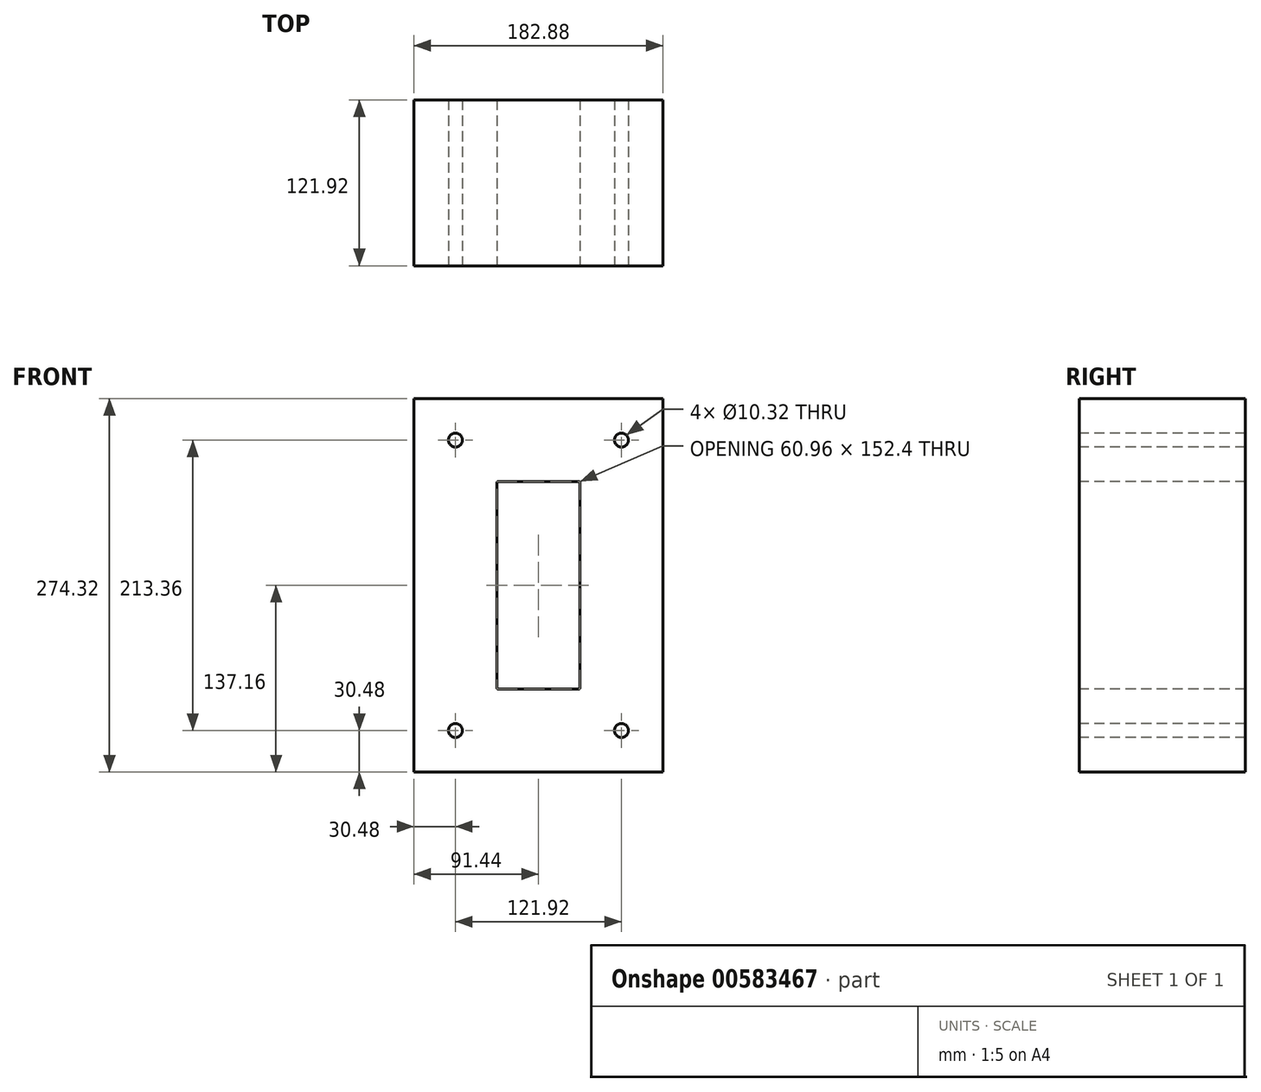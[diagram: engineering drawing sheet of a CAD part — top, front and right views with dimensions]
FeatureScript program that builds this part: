
annotation { "Feature Type Name" : "Feature", "Feature Type Description" : "" }
export const myFeature = defineFeature(function(context is Context, id is Id, definition is map)
    precondition{}
    {
        {
            assignVariable(context, id + "F0", {"name" : "StackHeight", "anyValue" : 121.92 * mm});
        }
        {
            var Q0;
            Q0=qCreatedBy(makeId("Front.planeOp"),FACE);
            var sketch = newSketch(context, id + "F1", { "sketchPlane" : qUnion([Q0])});
            skLineSegment(sketch, "E0.bottom", {"start": v(91.44, -137.16) * mm, "end": v(-91.44, -137.16) * mm});
            skLineSegment(sketch, "E0.top", {"start": v(91.44, 137.16) * mm, "end": v(-91.44, 137.16) * mm});
            skLineSegment(sketch, "E0.left", {"start": v(91.44, -137.16) * mm, "end": v(91.44, 137.16) * mm});
            skLineSegment(sketch, "E0.right", {"start": v(-91.44, -137.16) * mm, "end": v(-91.44, 137.16) * mm});
            skPoint(sketch, "E0.middle", {"position": v(0, 0) * mm});
            skSolve(sketch);
        }
        {
            var Q0;
            Q0=qSketchRegion(id+"F1",true);
            extrude(context, id + "F2", {"entities" : qUnion([Q0]), "oppositeDirection" : true, "depth" : (getVariable(context, 'StackHeight'))});
        }
        {
            var Q0;
            Q0=makeQuery(id+"F2.opExtrude","CAP_FACE",FACE,{"disambiguationData":[OSD([sQuery(id+"F1.wireOp",EDGE,"E0.bottom"),sQuery(id+"F1.wireOp",EDGE,"E0.top"),sQuery(id+"F1.wireOp",EDGE,"E0.left"),sQuery(id+"F1.wireOp",EDGE,"E0.right")])],"isStart":true});
            var sketch = newSketch(context, id + "F3", { "sketchPlane" : qUnion([Q0])});
            skCircle(sketch, "E1", {"center": v(-60.96, 106.68) * mm, "radius": 5.16 * mm});
            skCircle(sketch, "E2", {"center": v(60.96, 106.68) * mm, "radius": 5.16 * mm});
            skCircle(sketch, "E3", {"center": v(-60.96, -106.68) * mm, "radius": 5.16 * mm});
            skCircle(sketch, "E4", {"center": v(60.96, -106.68) * mm, "radius": 5.16 * mm});
            skSolve(sketch);
        }
        {
            var Q0;
            Q0=qSketchRegion(id+"F3",true);
            extrude(context, id + "F4", {"entities" : qUnion([Q0]), "operationType" : NewBodyOperationType.REMOVE, "oppositeDirection" : true, "depth" : (getVariable(context, 'StackHeight'))});
        }
        {
            var Q0;
            Q0=makeQuery(id+"F2.opExtrude","CAP_FACE",FACE,{"disambiguationData":[OSD([sQuery(id+"F1.wireOp",EDGE,"E0.bottom"),sQuery(id+"F1.wireOp",EDGE,"E0.top"),sQuery(id+"F1.wireOp",EDGE,"E0.left"),sQuery(id+"F1.wireOp",EDGE,"E0.right")])],"isStart":true});
            var sketch = newSketch(context, id + "F5", { "sketchPlane" : qUnion([Q0])});
            skLineSegment(sketch, "E5.bottom", {"start": v(-30.48, -76.2) * mm, "end": v(30.48, -76.2) * mm});
            skLineSegment(sketch, "E5.top", {"start": v(-30.48, 76.2) * mm, "end": v(30.48, 76.2) * mm});
            skLineSegment(sketch, "E5.left", {"start": v(-30.48, -76.2) * mm, "end": v(-30.48, 76.2) * mm});
            skLineSegment(sketch, "E5.right", {"start": v(30.48, -76.2) * mm, "end": v(30.48, 76.2) * mm});
            skPoint(sketch, "E5.middle", {"position": v(0, 0) * mm});
            skSolve(sketch);
        }
        {
            var Q0;
            Q0=qSketchRegion(id+"F5",true);
            extrude(context, id + "F6", {"entities" : qUnion([Q0]), "operationType" : NewBodyOperationType.REMOVE, "oppositeDirection" : true, "depth" : (getVariable(context, 'StackHeight'))});
        }
        {
            var Q0;
            Q0=makeQuery(id+"F6.boolean.opBoolean","COPY",EDGE,{"derivedFrom":makeQuery(id+"F6.opExtrude","SWEPT_EDGE",EDGE,{"disambiguationData":[OSD([sQuery(id+"F5.wireOp",EDGE,"E5.top"),sQuery(id+"F5.wireOp",EDGE,"E5.left")])]})});
            var Q1;
            Q1=makeQuery(id+"F6.boolean.opBoolean","COPY",EDGE,{"derivedFrom":makeQuery(id+"F6.opExtrude","SWEPT_EDGE",EDGE,{"disambiguationData":[OSD([sQuery(id+"F5.wireOp",EDGE,"E5.top"),sQuery(id+"F5.wireOp",EDGE,"E5.right")])]})});
            var Q2;
            Q2=makeQuery(id+"F6.boolean.opBoolean","COPY",EDGE,{"derivedFrom":makeQuery(id+"F6.opExtrude","SWEPT_EDGE",EDGE,{"disambiguationData":[OSD([sQuery(id+"F5.wireOp",EDGE,"E5.bottom"),sQuery(id+"F5.wireOp",EDGE,"E5.right")])]})});
            var Q3;
            Q3=makeQuery(id+"F6.boolean.opBoolean","COPY",EDGE,{"derivedFrom":makeQuery(id+"F6.opExtrude","SWEPT_EDGE",EDGE,{"disambiguationData":[OSD([sQuery(id+"F5.wireOp",EDGE,"E5.bottom"),sQuery(id+"F5.wireOp",EDGE,"E5.left")])]})});
            fillet(context, id + "F7", {"entities" : qUnion([Q0, Q1, Q2, Q3]), "radius" : 0.8 * mm, "tangentPropagation" : true, "allowEdgeOverflow" : false});
        }
    });
